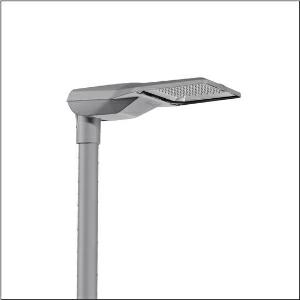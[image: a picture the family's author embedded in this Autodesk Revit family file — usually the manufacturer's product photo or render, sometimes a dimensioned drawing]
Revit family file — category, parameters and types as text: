
# Revit family: streetlight_sl_21_iq_midi___st1_0a_5xe3d41d08mb_7520
name_source: partatom
category: Lighting Fixtures
units: mm (PartAtom-declared; Revit-internal decimal feet)

## family parameters
Cut with Voids When Loaded = No
Host = Face
Light Source = No
Part Type = Normal
Room Calculation Point = No
Round Connector Dimension = Use Diameter
Shared = No

## types (1)
- --- (1 x LED, 20360 lm, 146.7 W, 4000K)
    Apparent Load = 147 VA
    CIE Flux Codes = 37 72 97 100 100
    Color Rendering = 70
    Color Temperature = 4000K
    Default Elevation = 1800 mm
    Description = Streetlight SL 21 iQ midi, mast luminaire, primary light control with lens, of PMMA, primary optical cover: cover, of toughened safety glass, transparent, light distribution: ST1.0a, light emission: direct distribution, primary light characteristic: asymmetric, installation type: post-top, side-entry, LED, High Power LED, rated luminous flux: 20.360lm, luminous efficacy: 139lm/W, light colour: 740, colour temperature: 4000K, control: Auto-Match, Temp-Guard, Lumen-Switch, Night-Set, Smart-Wire, Light-Fading, Desk-Remote (wireless, voltage-free reading and setting of iQ features in the workshop via application-optimized NFC function/RFID function), optimised constant luminous flux control (CLO 2.0), pre-setting: linear dimming characteristic, mains connection: 230..240V, AC, 50/60Hz, start of lifetime: 147W, end of service life: 161W, reduction: 62W, luminaire housing, of diecast aluminium, powder-coated, Siteco® metallic grey (DB 702S), corrosivity category C5 mid according to DIN EN ISO 12944, please order mast flange separately, inclination adjustable: 0°, 5°, 10°, 15°, sealing non-destructively replaceable, multi-level sealing system, length: 644mm, width: 335mm, height: 110mm, mast flange for spigot size: 42mm (side-entry): 5XC10008XM4, 60/48mm (side-entry/post-top): 5XC10108XM2, 76/60mm (side-entry/post-top): 5XC10108XM1, protection rating (complete): IP66, insulation class (complete): insulation class II (safety insulation), certification: CE, ENEC, ENEC+, VDE, impact resistance: IK09, permissible operating ambient temperature for outdoor applications: -40..+50°C, standard-compliant lighting for roads and squares, packaging unit: 1 piece

Light Distribution: ST1.0a
    Height = 111 mm
    Lamp = 1 x LED
    Lamp Light Flux = 20360 lm
    Lamp Power = 146.7 W
    Lamp count = 1
    Length = 644 mm
    Luminous efficacy = 139 lm/W
    Manufacturer = Siteco
    ModVariant = No
    Model = 5XE3D41D08MB
    Number of Poles = 1
    OnlyDefault = Yes
    Power Factor = 1
    Product Name = Streetlight SL 21 iQ midi | ST1.0a
    Product group = mast luminaire | pylon top
    ProductGroupID = 6100
    Protection Class = Protection class II
    Protection Degree = IP 66
    RLX_Detail_Level = 1
    RLX_Emergency_Light_Flux = 0 lm
    RLX_Emergency_Type = 0
    RLX_Emergency_Type_DB = No
    RlxData = <blob elided: 90765 chars, md5=c4222f8c>
    Socket = socket
    Standby Power = 0 W
    System Light Flux = 20360 lm
    System Power = 147 W
    Type Comments = factory setting: luminous flux: 100 % | dim-lin: 254 | 753 mA
    Type Image = l_1004298.jpg
    URL = http://relux.com
    VarID = @adj_161837
    Voltage = 0 V
    Weight = 0.00 kg
    Width = 336 mm

## geometry (parser evidence)
native form markers: Blend x4, Sweep x13
no freeform markers — native parametric forms only
